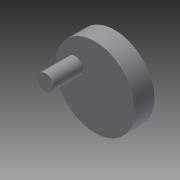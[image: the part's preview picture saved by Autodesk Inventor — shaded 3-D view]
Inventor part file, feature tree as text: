
AUTODESK INVENTOR PART (.ipt)
format: ipt  version: 2014 (Build 180170000, 170)  size: 81,920 bytes
history: native  units: in
note: dims shown in document units (in); Inventor stores cm internally (conversion verified against a paired STEP export)
features: extrude x2, sketch x2
ambient origin geometry x8: Origin, YZ Plane, XZ Plane, XY Plane, X Axis, Y Axis, Z Axis, Center Point
bodies: Solid1 (feature_tree)
feature tree (4):
  extrude  "Extrusion1"  Depth=0.5in TaperAngle=0.0deg
  extrude  "Extrusion2"  Depth=0.5in
  sketch  "Sketch1"  dims[d0=2.0in d1=0.5in d2=0.0in]
  sketch  "Sketch2"  dims[d3=0.4in d4=0.5in d5=0.23in d6=0.75in d7=0.0in]
